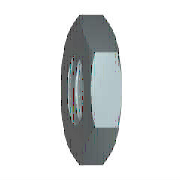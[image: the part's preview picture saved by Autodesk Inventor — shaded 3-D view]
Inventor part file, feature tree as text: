
AUTODESK INVENTOR PART (.ipt)
format: ipt  version: 2025 (Build 290162010, 162A)  size: 164,352 bytes
history: native  units: mm (DEFAULTED — no unit token found)
features: chamfer x1, hole x1, other x1, plane x1
ambient origin geometry x7: Origin, YZ Plane, XZ Plane, X Axis, Y Axis, Z Axis, Center Point
bodies: Solid1 (feature_tree), Body (feature_tree)
feature tree (4):
  chamfer  "Chamfer1"  Distance=6.350853mm
  hole  "Thread"  [1 undecoded]
  other  "Work Axis1"
  plane  "Work Plane1"
note: 1 required parameter value undecoded (feature->parameter linkage not recoverable at this tier; creation-order binding heuristic only, values carry confidence <= 0.55)
